# Revit family: QF_EVEREST_EMGR5
name_source: partatom
category: Specialty Equipment
revit_build: Autodesk Revit 2015 (Build: 20140606_1530(x64)
units: mm (PartAtom-declared; Revit-internal decimal feet)

## types (1)
- QF_EVEREST_EMGR5
    Apparent Power = 230 VA
    BTUH = 0.0 Btu/h
    Conn Conduit = Yes
    Conn Plug = NEMA 5-15P
    Cycle = 60 Hz
    Depth = 628 mm  [stored 2.06037 ft]
    Description = GLASS DOOR MERCHANDISER REFRIGERATOR
    Elec Conn Connection Height = 0 mm  [stored 0 ft]
    Elec Conn RI Height = 0 mm  [stored 0 ft]
    FL Amps = 2 A
    Foodservice Equipment Identifier = Yes
    HP = 1/5
    Height = 936 mm  [stored 3.07087 ft]
    Identify Quantity as Lot = Yes
    Length = 635 mm  [stored 2.08333 ft]
    Manufacturer = EVEREST
    Max Overcurrent Protection = 0 A
    Min Ckt Ampacity = 0 A
    Model = EMGR5
    Number of Poles = 1
    Phase = 1
    Refrigerant Type = R290
    Refrigerant Volume = 0.00 kip
    Volts = 115 V
    Watts = 230 W
    Weight in Pounds = 192

note: [stored X ft] marks values corroborated as IEEE doubles in the binary element streams (Revit-internal decimal feet)

## geometry (parser evidence)
native form markers: Sweep x8
no freeform markers — native parametric forms only
